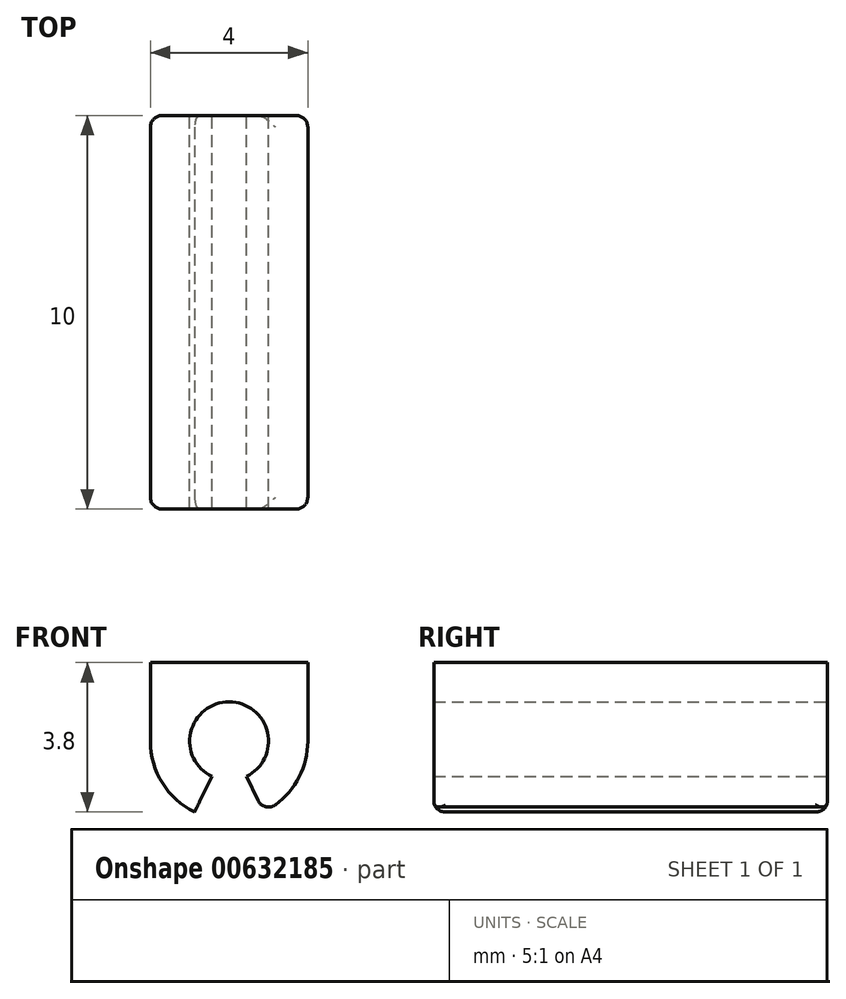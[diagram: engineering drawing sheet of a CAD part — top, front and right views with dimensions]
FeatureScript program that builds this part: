
annotation { "Feature Type Name" : "Feature", "Feature Type Description" : "" }
export const myFeature = defineFeature(function(context is Context, id is Id, definition is map)
    precondition{}
    {
        {
            var Q0;
            Q0=qCreatedBy(makeId("Front.planeOp"),FACE);
            var sketch = newSketch(context, id + "F0", { "sketchPlane" : qUnion([Q0])});
            skCircle(sketch, "E0", {"center": v(0, 0) * mm, "radius": 1 * mm});
            skArc(sketch, "E1", {"start": v(-2, 0) * mm, "mid": v(0, -2) * mm, "end": v(2, 0) * mm});
            skLineSegment(sketch, "E2", {"start": v(-2, 0) * mm, "end": v(-2, 2) * mm});
            skLineSegment(sketch, "E3", {"start": v(-2, 2) * mm, "end": v(0, 2) * mm});
            skLineSegment(sketch, "E4.MirrorCS", {"start": v(2, 2) * mm, "end": v(0, 2) * mm});
            skLineSegment(sketch, "E5.MirrorCS", {"start": v(2, 0) * mm, "end": v(2, 2) * mm});
            skSolve(sketch);
        }
        {
            var Q0;
            Q0=makeQuery(id+"F0.imprint","IMPRINT",FACE,{"disambiguationData":[TD([[makeQuery(id+"F0.imprint","IMPRINT",EDGE,{"derivedFrom":sQuery(id+"F0.wireOp",EDGE,"E0")}),-1.0]])]});
            extrude(context, id + "F1", {"entities" : qUnion([Q0]), "endBound" : BoundingType.SYMMETRIC, "depth" : 10 * mm, "offsetDistance" : 25.4 * mm});
        }
        {
            var Q0;
            Q0=makeQuery(id+"F1.opExtrude","CAP_FACE",FACE,{"disambiguationData":[OSD([sQuery(id+"F0.wireOp",EDGE,"E0"),sQuery(id+"F0.wireOp",EDGE,"E1")])],"isStart":false});
            var sketch = newSketch(context, id + "F2", { "sketchPlane" : qUnion([Q0])});
            skLineSegment(sketch, "E6", {"start": v(0, 0) * mm, "end": v(-0.87, -1.8) * mm});
            skLineSegment(sketch, "E7.MirrorCS", {"start": v(0, 0) * mm, "end": v(0.87, -1.8) * mm});
            skArc(sketch, "E8", {"start": v(-0.87, -1.8) * mm, "mid": v(0, -2) * mm, "end": v(0.87, -1.8) * mm});
            skSolve(sketch);
        }
        {
            var Q0;
            Q0 = qSketchRegion(id + "F2", true);
            extrude(context, id + "F3", {"entities" : qUnion([Q0]), "operationType" : NewBodyOperationType.REMOVE, "endBound" : BoundingType.THROUGH_ALL, "oppositeDirection" : true, "depth" : 25 * mm, "offsetDistance" : 25 * mm});
        }
        {
            var Q0;
            Q0=makeQuery(id+"F3.boolean.opBoolean","COPY",EDGE,{"derivedFrom":makeQuery(id+"F3.opExtrude","SWEPT_EDGE",EDGE,{"disambiguationData":[OSD([sQuery(id+"F0.wireOp",EDGE,"E1"),sQuery(id+"F2.wireOp",EDGE,"E6"),sQuery(id+"F2.wireOp",EDGE,"E8")])]})});
            var Q1;
            Q1=makeQuery(id+"F3.boolean.opBoolean","COPY",EDGE,{"derivedFrom":makeQuery(id+"F3.opExtrude","SWEPT_EDGE",EDGE,{"disambiguationData":[OSD([sQuery(id+"F0.wireOp",EDGE,"E1"),sQuery(id+"F2.wireOp",EDGE,"E7.MirrorCS"),sQuery(id+"F2.wireOp",EDGE,"E8")])]})});
            var Q2;
            {var subQ0=sQuery(id+"F0.wireOp",EDGE,"E2");var subQ1=sQuery(id+"F0.wireOp",EDGE,"E1");Q2=makeQuery(id+"F3.boolean.opBoolean","SPLIT",EDGE,{"disambiguationData":[TD([makeQuery(id+"F1.opExtrude","SWEPT_FACE",FACE,{"disambiguationData":[OSD([subQ0])]})])],"derivedFrom":makeQuery(id+"F1.opExtrude","CAP_EDGE",EDGE,{"disambiguationData":[OSD([subQ1])],"isStart":false})});}
            var Q3;
            Q3=makeQuery(id+"F1.opExtrude","CAP_EDGE",EDGE,{"disambiguationData":[OSD([sQuery(id+"F0.wireOp",EDGE,"E2")])],"isStart":false});
            var Q4;
            {var subQ0=sQuery(id+"F0.wireOp",EDGE,"E5.MirrorCS");var subQ1=sQuery(id+"F0.wireOp",EDGE,"E1");Q4=makeQuery(id+"F3.boolean.opBoolean","SPLIT",EDGE,{"disambiguationData":[TD([makeQuery(id+"F1.opExtrude","SWEPT_FACE",FACE,{"disambiguationData":[OSD([subQ0])]})])],"derivedFrom":makeQuery(id+"F1.opExtrude","CAP_EDGE",EDGE,{"disambiguationData":[OSD([subQ1])],"isStart":false})});}
            var Q5;
            {var subQ0=sQuery(id+"F0.wireOp",EDGE,"E5.MirrorCS");var subQ1=sQuery(id+"F0.wireOp",EDGE,"E1");Q5=makeQuery(id+"F3.boolean.opBoolean","SPLIT",EDGE,{"disambiguationData":[TD([makeQuery(id+"F1.opExtrude","SWEPT_FACE",FACE,{"disambiguationData":[OSD([subQ0])]})])],"derivedFrom":makeQuery(id+"F1.opExtrude","CAP_EDGE",EDGE,{"disambiguationData":[OSD([subQ1])],"isStart":true})});}
            var Q6;
            Q6=makeQuery(id+"F1.opExtrude","CAP_EDGE",EDGE,{"disambiguationData":[OSD([sQuery(id+"F0.wireOp",EDGE,"E5.MirrorCS")])],"isStart":true});
            var Q7;
            {var subQ0=sQuery(id+"F0.wireOp",EDGE,"E2");var subQ1=sQuery(id+"F0.wireOp",EDGE,"E1");Q7=makeQuery(id+"F3.boolean.opBoolean","SPLIT",EDGE,{"disambiguationData":[TD([makeQuery(id+"F1.opExtrude","SWEPT_FACE",FACE,{"disambiguationData":[OSD([subQ0])]})])],"derivedFrom":makeQuery(id+"F1.opExtrude","CAP_EDGE",EDGE,{"disambiguationData":[OSD([subQ1])],"isStart":true})});}
            var Q8;
            Q8=makeQuery(id+"F1.opExtrude","CAP_EDGE",EDGE,{"disambiguationData":[OSD([sQuery(id+"F0.wireOp",EDGE,"E2")])],"isStart":true});
            fillet(context, id + "F4", {"entities" : qUnion([Q0, Q1, Q2, Q3, Q4, Q5, Q6, Q7, Q8]), "radius" : .3 * mm, "tangentPropagation" : true, "allowEdgeOverflow" : false});
        }
    });
